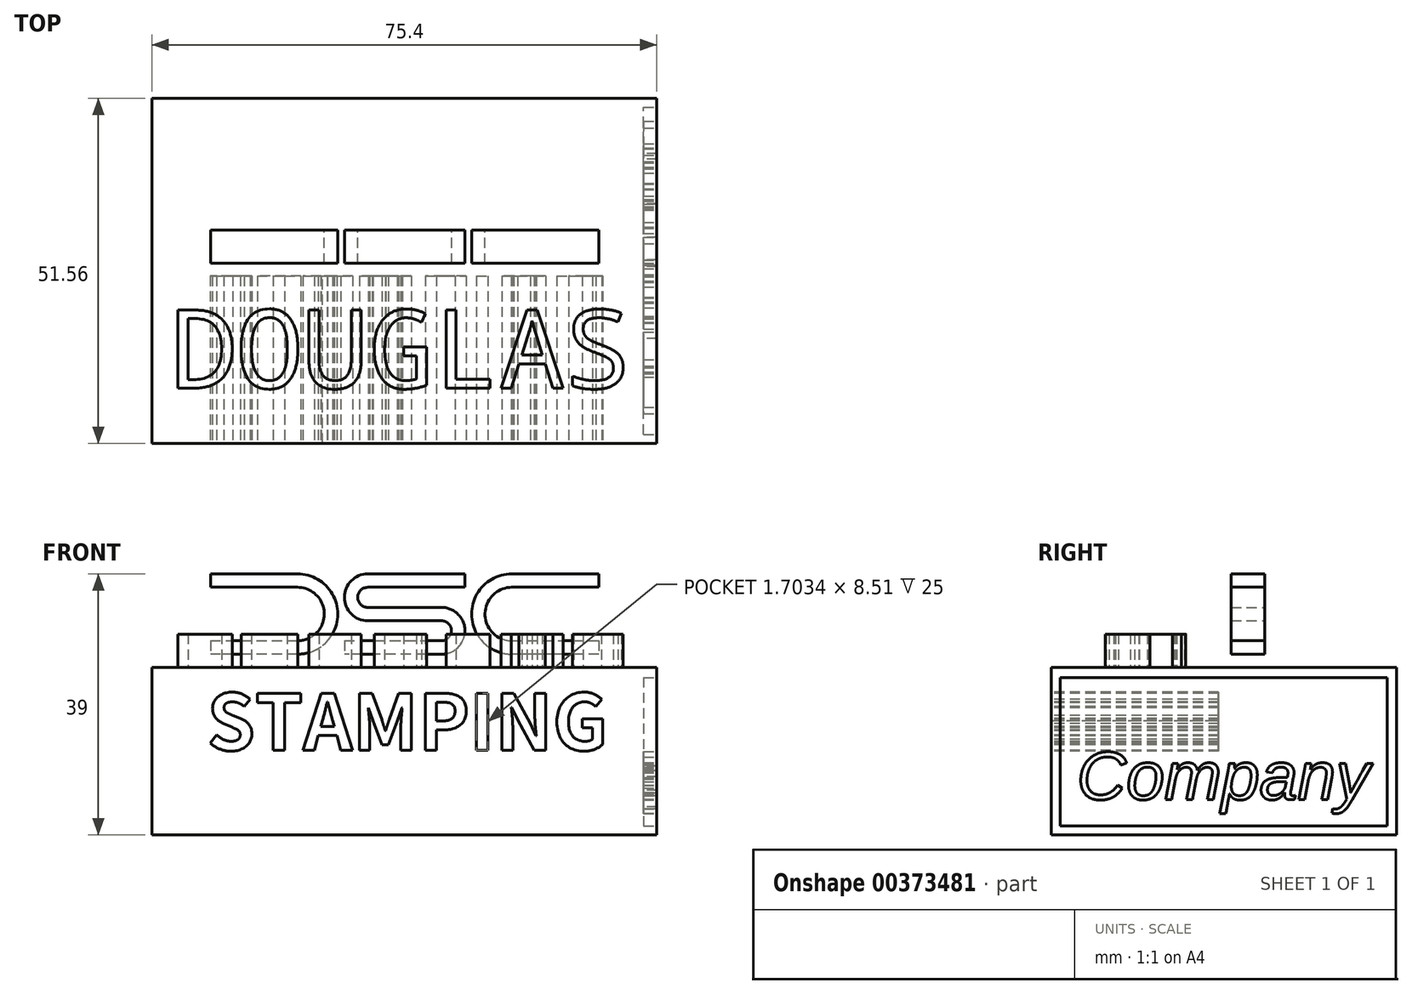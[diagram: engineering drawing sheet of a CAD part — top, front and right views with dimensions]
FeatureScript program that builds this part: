
annotation { "Feature Type Name" : "Feature", "Feature Type Description" : "" }
export const myFeature = defineFeature(function(context is Context, id is Id, definition is map)
    precondition{}
    {
        {
            var Q0;
            Q0=qCreatedBy(makeId("Front.planeOp"),FACE);
            var sketch = newSketch(context, id + "F0", { "sketchPlane" : qUnion([Q0])});
            skLineSegment(sketch, "E0.bottom", {"start": v(24, 6) * mm, "end": v(11, 6) * mm});
            skLineSegment(sketch, "E0.top", {"start": v(24, -6) * mm, "end": v(11, -6) * mm});
            skLineSegment(sketch, "E0.left", {"start": v(30, 0) * mm, "end": v(30, 0) * mm});
            skLineSegment(sketch, "E0.right", {"start": v(-30, 0) * mm, "end": v(-30, 0) * mm});
            skPoint(sketch, "E0.middle", {"position": v(0, 0) * mm});
            skPoint(sketch, "E1.visualSharp", {"position": v(-30, 6) * mm});
            skArc(sketch, "E1.filletArc", {"start": v(-24, 6) * mm, "mid": v(-28.24, 4.24) * mm, "end": v(-30, 0) * mm});
            skPoint(sketch, "E2.visualSharp", {"position": v(-30, -6) * mm});
            skArc(sketch, "E2.filletArc", {"start": v(-30, 0) * mm, "mid": v(-28.24, -4.24) * mm, "end": v(-24, -6) * mm});
            skPoint(sketch, "E3.visualSharp", {"position": v(30, 6) * mm});
            skArc(sketch, "E3.filletArc", {"start": v(30, 0) * mm, "mid": v(28.24, 4.24) * mm, "end": v(24, 6) * mm});
            skPoint(sketch, "E4.visualSharp", {"position": v(30, -6) * mm});
            skArc(sketch, "E4.filletArc", {"start": v(24, -6) * mm, "mid": v(28.24, -4.24) * mm, "end": v(30, 0) * mm});
            skArc(sketch, "E5.0", {"start": v(-24, 4) * mm, "mid": v(-26.83, 2.83) * mm, "end": v(-28, 0) * mm});
            skArc(sketch, "E6.MirrorCS", {"start": v(-24, -4) * mm, "mid": v(-26.83, -2.83) * mm, "end": v(-28, 0) * mm});
            skArc(sketch, "E7.MirrorCS", {"start": v(24, 4) * mm, "mid": v(26.83, 2.83) * mm, "end": v(28, 0) * mm});
            skArc(sketch, "E8.MirrorCS", {"start": v(24, -4) * mm, "mid": v(26.83, -2.83) * mm, "end": v(28, 0) * mm});
            skLineSegment(sketch, "E9", {"start": v(-24, 4) * mm, "end": v(-11, 4) * mm});
            skLineSegment(sketch, "E10", {"start": v(-24, -4) * mm, "end": v(-11, -4) * mm});
            skLineSegment(sketch, "E11", {"start": v(-11, 6) * mm, "end": v(-11, 4) * mm});
            skLineSegment(sketch, "E12.MirrorCS", {"start": v(11, 6) * mm, "end": v(11, 4) * mm});
            skLineSegment(sketch, "E13.trimOffspring", {"start": v(-11, 6) * mm, "end": v(-24, 6) * mm});
            skLineSegment(sketch, "E14.trimOffspring", {"start": v(-5.5, 4) * mm, "end": v(9, 4) * mm});
            skLineSegment(sketch, "E15.trimOffspring", {"start": v(-11, -4) * mm, "end": v(-11, -6) * mm});
            skLineSegment(sketch, "E16.trimOffspring", {"start": v(-9, -4) * mm, "end": v(5.5, -4) * mm});
            skLineSegment(sketch, "E17.trimOffspring", {"start": v(-11, -6) * mm, "end": v(-24, -6) * mm});
            skLineSegment(sketch, "E18.trimOffspring", {"start": v(9, 6) * mm, "end": v(-5.5, 6) * mm});
            skLineSegment(sketch, "E19.trimOffspring", {"start": v(11, 4) * mm, "end": v(24, 4) * mm});
            skLineSegment(sketch, "E20.trimOffspring", {"start": v(11, -4) * mm, "end": v(24, -4) * mm});
            skLineSegment(sketch, "E21.trimOffspring", {"start": v(5.5, -6) * mm, "end": v(-9, -6) * mm});
            skLineSegment(sketch, "E22.trimOffspring", {"start": v(11, -4) * mm, "end": v(11, -6) * mm});
            skLineSegment(sketch, "E23.MirrorCS", {"start": v(-5.5, -1) * mm, "end": v(5.5, -1) * mm});
            skLineSegment(sketch, "E24", {"start": v(-9, 2.5) * mm, "end": v(9, 2.5) * mm, "construction": true});
            skLineSegment(sketch, "E25", {"start": v(-9, -2.5) * mm, "end": v(9, -2.5) * mm, "construction": true});
            skArc(sketch, "E26", {"start": v(-5.5, 6) * mm, "mid": v(-9, 2.5) * mm, "end": v(-5.5, -1) * mm});
            skArc(sketch, "E27", {"start": v(-5.5, 4) * mm, "mid": v(-7, 2.5) * mm, "end": v(-5.5, 1) * mm});
            skArc(sketch, "E28", {"start": v(5.5, -6) * mm, "mid": v(9, -2.5) * mm, "end": v(5.5, 1) * mm});
            skArc(sketch, "E29", {"start": v(5.5, -4) * mm, "mid": v(7, -2.5) * mm, "end": v(5.5, -1) * mm});
            skPoint(sketch, "E30.orphan", {"position": v(-9, 6) * mm});
            skPoint(sketch, "E31.orphan", {"position": v(-9, 4) * mm});
            skLineSegment(sketch, "E32.trimOffspring", {"start": v(-5.5, 1) * mm, "end": v(5.5, 1) * mm});
            skPoint(sketch, "E33.start.orphan", {"position": v(-9, 1) * mm});
            skLineSegment(sketch, "E34", {"start": v(9, 6) * mm, "end": v(9, 4) * mm});
            skLineSegment(sketch, "E35", {"start": v(-9, -4) * mm, "end": v(-9, -6) * mm});
            skPoint(sketch, "E36.orphan", {"position": v(-9, -1) * mm});
            skPoint(sketch, "E37.start.orphan", {"position": v(9, 1) * mm});
            skPoint(sketch, "E38.orphan", {"position": v(9, -6) * mm});
            skPoint(sketch, "E39.orphan", {"position": v(9, -1) * mm});
            skPoint(sketch, "E40.orphan", {"position": v(9, -4) * mm});
            skSolve(sketch);
        }
        {
            var Q0;
            Q0=makeQuery(id+"F0.imprint","IMPRINT",FACE,{"disambiguationData":[TD([[makeQuery(id+"F0.imprint","IMPRINT",EDGE,{"derivedFrom":sQuery(id+"F0.wireOp",EDGE,"E1.filletArc")}),1.0]])]});
            var Q1;
            Q1=makeQuery(id+"F0.imprint","IMPRINT",FACE,{"disambiguationData":[TD([[makeQuery(id+"F0.imprint","IMPRINT",EDGE,{"derivedFrom":sQuery(id+"F0.wireOp",EDGE,"E14.trimOffspring")}),1.0]])]});
            var Q2;
            Q2=makeQuery(id+"F0.imprint","IMPRINT",FACE,{"disambiguationData":[TD([[makeQuery(id+"F0.imprint","IMPRINT",EDGE,{"derivedFrom":sQuery(id+"F0.wireOp",EDGE,"E0.bottom")}),1.0]])]});
            extrude(context, id + "F1", {"entities" : qUnion([Q0, Q1, Q2]), "depth" : 5 * mm});
        }
        {
            var Q0;
            Q0=makeQuery(id+"F1.opExtrude","SWEPT_BODY",BODY,{"disambiguationData":[OSD([sQuery(id+"F0.wireOp",EDGE,"E1.filletArc"),sQuery(id+"F0.wireOp",EDGE,"E2.filletArc"),sQuery(id+"F0.wireOp",EDGE,"E6.MirrorCS"),sQuery(id+"F0.wireOp",EDGE,"E5.0"),sQuery(id+"F0.wireOp",EDGE,"E9"),sQuery(id+"F0.wireOp",EDGE,"E10"),sQuery(id+"F0.wireOp",EDGE,"E11"),sQuery(id+"F0.wireOp",EDGE,"E13.trimOffspring"),sQuery(id+"F0.wireOp",EDGE,"E15.trimOffspring"),sQuery(id+"F0.wireOp",EDGE,"E17.trimOffspring")])]});
            var Q1;
            Q1=makeQuery(id+"F1.opExtrude","CAP_EDGE",EDGE,{"disambiguationData":[OSD([sQuery(id+"F0.wireOp",EDGE,"E10")])],"isStart":false});
            transform(context, id + "F2", {"entities" : qUnion([Q0]), "transformType" : TransformType.TRANSLATION_DISTANCE, "transformDirection" : qUnion([Q1]), "distance" : 40 * mm, "makeCopy" : false});
        }
        {
            var Q0;
            Q0=makeQuery(id+"F1.opExtrude","SWEPT_BODY",BODY,{"disambiguationData":[OSD([sQuery(id+"F0.wireOp",EDGE,"E0.bottom"),sQuery(id+"F0.wireOp",EDGE,"E0.top"),sQuery(id+"F0.wireOp",EDGE,"E3.filletArc"),sQuery(id+"F0.wireOp",EDGE,"E4.filletArc"),sQuery(id+"F0.wireOp",EDGE,"E7.MirrorCS"),sQuery(id+"F0.wireOp",EDGE,"E8.MirrorCS"),sQuery(id+"F0.wireOp",EDGE,"E12.MirrorCS"),sQuery(id+"F0.wireOp",EDGE,"E19.trimOffspring"),sQuery(id+"F0.wireOp",EDGE,"E20.trimOffspring"),sQuery(id+"F0.wireOp",EDGE,"E22.trimOffspring")])]});
            var Q1;
            Q1=makeQuery(id+"F1.opExtrude","CAP_EDGE",EDGE,{"disambiguationData":[OSD([sQuery(id+"F0.wireOp",EDGE,"E16.trimOffspring")])],"isStart":false});
            transform(context, id + "F3", {"entities" : qUnion([Q0]), "transformType" : TransformType.TRANSLATION_DISTANCE, "transformDirection" : qUnion([Q1]), "distance" : 40 * mm, "oppositeDirection" : true, "makeCopy" : false});
        }
        {
            var Q0;
            Q0=makeQuery(id+"F1.opExtrude","SWEPT_BODY",BODY,{"disambiguationData":[OSD([sQuery(id+"F0.wireOp",EDGE,"E0.bottom"),sQuery(id+"F0.wireOp",EDGE,"E0.top"),sQuery(id+"F0.wireOp",EDGE,"E3.filletArc"),sQuery(id+"F0.wireOp",EDGE,"E4.filletArc"),sQuery(id+"F0.wireOp",EDGE,"E7.MirrorCS"),sQuery(id+"F0.wireOp",EDGE,"E8.MirrorCS"),sQuery(id+"F0.wireOp",EDGE,"E12.MirrorCS"),sQuery(id+"F0.wireOp",EDGE,"E19.trimOffspring"),sQuery(id+"F0.wireOp",EDGE,"E20.trimOffspring"),sQuery(id+"F0.wireOp",EDGE,"E22.trimOffspring")])]});
            var Q1;
            Q1=makeQuery(id+"F1.opExtrude","SWEPT_BODY",BODY,{"disambiguationData":[OSD([sQuery(id+"F0.wireOp",EDGE,"E1.filletArc"),sQuery(id+"F0.wireOp",EDGE,"E2.filletArc"),sQuery(id+"F0.wireOp",EDGE,"E6.MirrorCS"),sQuery(id+"F0.wireOp",EDGE,"E5.0"),sQuery(id+"F0.wireOp",EDGE,"E9"),sQuery(id+"F0.wireOp",EDGE,"E10"),sQuery(id+"F0.wireOp",EDGE,"E11"),sQuery(id+"F0.wireOp",EDGE,"E13.trimOffspring"),sQuery(id+"F0.wireOp",EDGE,"E15.trimOffspring"),sQuery(id+"F0.wireOp",EDGE,"E17.trimOffspring")])]});
            var Q2;
            Q2=makeQuery(id+"F1.opExtrude","SWEPT_BODY",BODY,{"disambiguationData":[OSD([sQuery(id+"F0.wireOp",EDGE,"E14.trimOffspring"),sQuery(id+"F0.wireOp",EDGE,"E16.trimOffspring"),sQuery(id+"F0.wireOp",EDGE,"E18.trimOffspring"),sQuery(id+"F0.wireOp",EDGE,"E21.trimOffspring"),sQuery(id+"F0.wireOp",EDGE,"E23.MirrorCS"),sQuery(id+"F0.wireOp",EDGE,"E26"),sQuery(id+"F0.wireOp",EDGE,"E27"),sQuery(id+"F0.wireOp",EDGE,"E28"),sQuery(id+"F0.wireOp",EDGE,"E29"),sQuery(id+"F0.wireOp",EDGE,"E32.trimOffspring"),sQuery(id+"F0.wireOp",EDGE,"E34"),sQuery(id+"F0.wireOp",EDGE,"E35")])]});
            transform(context, id + "F4", {"entities" : qUnion([Q0, Q1, Q2]), "transformType" : TransformType.TRANSLATION_3D, "dx" : 0 * mm, "dy" : 0 * mm, "dz" : 8 * mm, "makeCopy" : false});
        }
        {
            var Q0;
            Q0=qCreatedBy(makeId("Top.planeOp"),FACE);
            var sketch = newSketch(context, id + "F5", { "sketchPlane" : qUnion([Q0])});
            skLineSegment(sketch, "E41.bottom", {"start": v(-37.74, 19.66) * mm, "end": v(37.66, 19.66) * mm});
            skLineSegment(sketch, "E41.top", {"start": v(-37.74, -31.9) * mm, "end": v(37.66, -31.9) * mm});
            skLineSegment(sketch, "E41.left", {"start": v(-37.74, 19.66) * mm, "end": v(-37.74, -31.9) * mm});
            skLineSegment(sketch, "E41.right", {"start": v(37.66, 19.66) * mm, "end": v(37.66, -31.9) * mm});
            skSolve(sketch);
        }
        {
            var Q0;
            Q0=makeQuery(id+"F5.imprint","IMPRINT",FACE,{"disambiguationData":[TD([[makeQuery(id+"F5.imprint","IMPRINT",EDGE,{"derivedFrom":sQuery(id+"F5.wireOp",EDGE,"E41.bottom")}),-1.0]])]});
            extrude(context, id + "F6", {"entities" : qUnion([Q0]), "oppositeDirection" : true, "depth" : 25 * mm});
        }
        {
            var Q0;
            Q0=makeQuery(id+"F6.opExtrude","CAP_FACE",FACE,{"disambiguationData":[OSD([sQuery(id+"F5.wireOp",EDGE,"E41.bottom"),sQuery(id+"F5.wireOp",EDGE,"E41.top"),sQuery(id+"F5.wireOp",EDGE,"E41.left"),sQuery(id+"F5.wireOp",EDGE,"E41.right")])],"isStart":true});
            var sketch = newSketch(context, id + "F7", { "sketchPlane" : qUnion([Q0])});
            skText(sketch, "E42", { "text": "DOUGLAS", "fontName": "DroidSansMono.ttf"});
            const initialGuessF7  = {"E42": [-0.03491, -0.02366, 1, 0, 0.01177]};
            skSetInitialGuess(sketch, initialGuessF7);
            skSolve(sketch);
        }
        {
            var Q0;
            Q0 = qSketchRegion(id + "F7", true);
            extrude(context, id + "F8", {"entities" : qUnion([Q0]), "operationType" : NewBodyOperationType.ADD, "depth" : 5 * mm});
        }
        {
            var Q0;
            Q0=makeQuery(id+"F6.opExtrude","SWEPT_FACE",FACE,{"disambiguationData":[OSD([sQuery(id+"F5.wireOp",EDGE,"E41.top")])]});
            var sketch = newSketch(context, id + "F9", { "sketchPlane" : qUnion([Q0])});
            skText(sketch, "E43", { "text": "STAMPING", "fontName": "NotoSansCJKsc-Bold.otf"});
            const initialGuessF9  = {"E43": [-0.02953, -0.01233, 1, 0, 0.00828]};
            skSetInitialGuess(sketch, initialGuessF9);
            skSolve(sketch);
        }
        {
            var Q0;
            Q0 = qSketchRegion(id + "F9", true);
            extrude(context, id + "F10", {"entities" : qUnion([Q0]), "operationType" : NewBodyOperationType.REMOVE, "oppositeDirection" : true, "depth" : 25 * mm});
        }
        {
            var Q0;
            Q0=makeQuery(id+"F6.opExtrude","SWEPT_FACE",FACE,{"disambiguationData":[OSD([sQuery(id+"F5.wireOp",EDGE,"E41.right")])]});
            var sketch = newSketch(context, id + "F11", { "sketchPlane" : qUnion([Q0])});
            skText(sketch, "E44", { "text": "Company", "fontName": "Arimo-Italic.ttf"});
            skPoint(sketch, "E44.firstSnap0", {"position": v(-25.57, -12.33) * mm});
            skLineSegment(sketch, "E45.bottom", {"start": v(-30.55, -1.47) * mm, "end": v(18.32, -1.47) * mm});
            skLineSegment(sketch, "E45.top", {"start": v(-30.55, -23.64) * mm, "end": v(18.32, -23.64) * mm});
            skLineSegment(sketch, "E45.left", {"start": v(-30.55, -1.47) * mm, "end": v(-30.55, -23.64) * mm});
            skLineSegment(sketch, "E45.right", {"start": v(18.32, -1.47) * mm, "end": v(18.32, -23.64) * mm});
            const initialGuessF11  = {"E44": [-0.02804, -0.0197, 1, 0, 0.00736]};
            skSetInitialGuess(sketch, initialGuessF11);
            skSolve(sketch);
        }
        {
            var Q0;
            Q0=makeQuery(id+"F11.imprint","IMPRINT",FACE,{"disambiguationData":[TD([[makeQuery(id+"F11.imprint","IMPRINT",EDGE,{"derivedFrom":sQuery(id+"F11.wireOp",EDGE,"E44.sketch_text.stroke-0")}),1.0]])]});
            var Q1;
            Q1=makeQuery(id+"F11.imprint","IMPRINT",FACE,{"disambiguationData":[TD([[makeQuery(id+"F11.imprint","IMPRINT",EDGE,{"derivedFrom":sQuery(id+"F11.wireOp",EDGE,"E44.sketch_text.stroke-94")}),1.0]])]});
            var Q2;
            Q2=makeQuery(id+"F11.imprint","IMPRINT",FACE,{"disambiguationData":[TD([[makeQuery(id+"F11.imprint","IMPRINT",EDGE,{"derivedFrom":sQuery(id+"F11.wireOp",EDGE,"E44.sketch_text.stroke-133")}),1.0]])]});
            var Q3;
            Q3=makeQuery(id+"F11.imprint","IMPRINT",FACE,{"disambiguationData":[TD([[makeQuery(id+"F11.imprint","IMPRINT",EDGE,{"derivedFrom":sQuery(id+"F11.wireOp",EDGE,"E44.sketch_text.stroke-32")}),1.0]])]});
            extrude(context, id + "F12", {"entities" : qUnion([Q0, Q1, Q2, Q3]), "operationType" : NewBodyOperationType.REMOVE, "oppositeDirection" : true, "depth" : 2 * mm});
        }
    });
